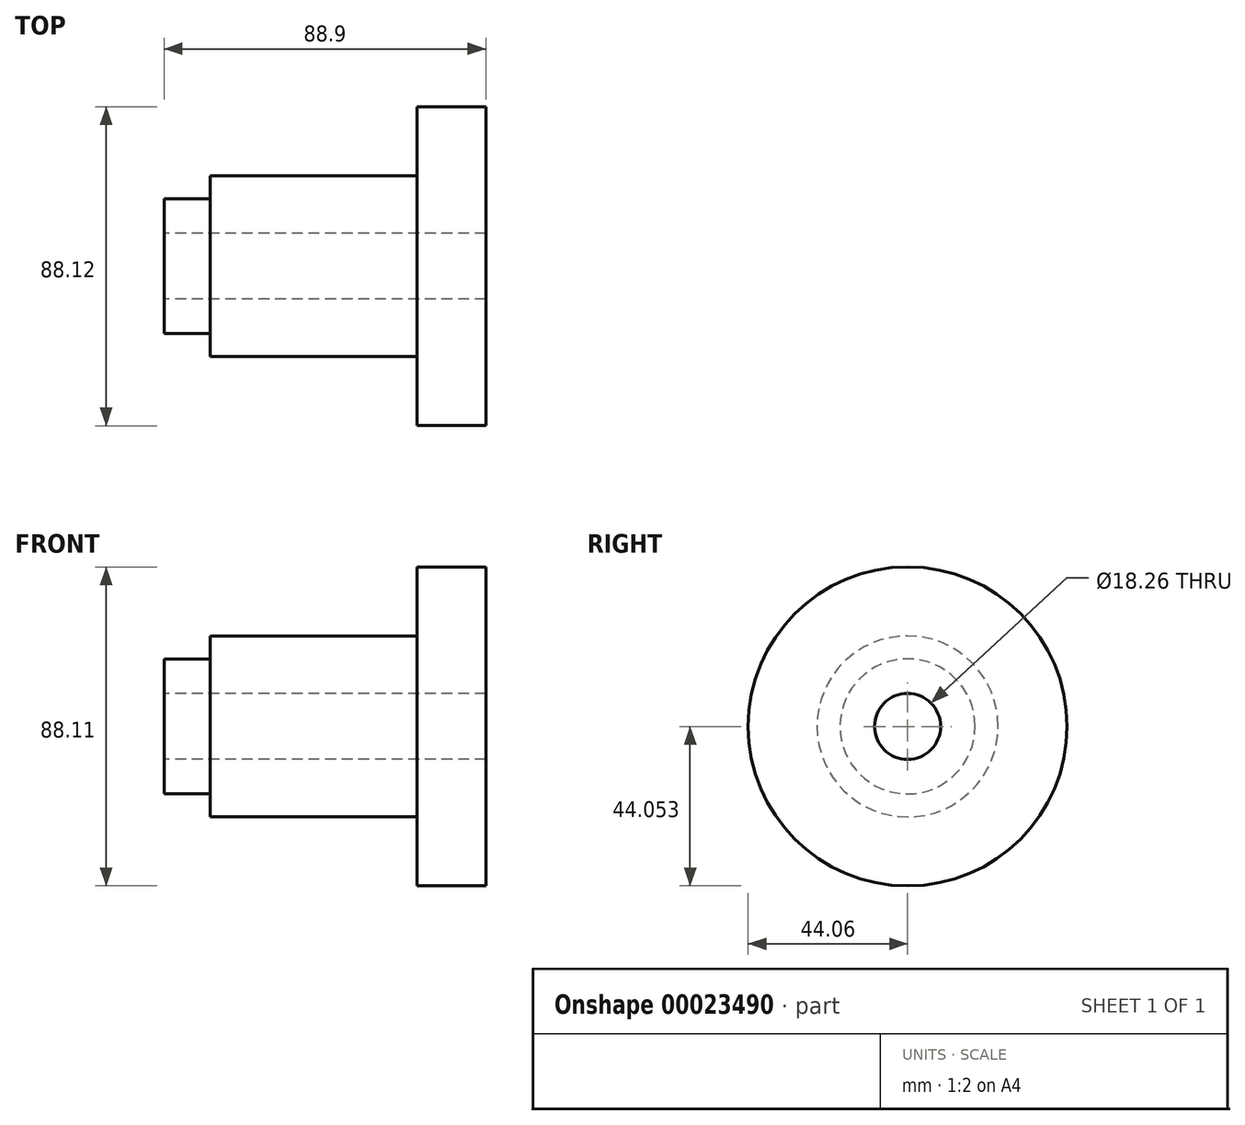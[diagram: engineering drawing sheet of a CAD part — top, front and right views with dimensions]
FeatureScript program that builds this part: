
annotation { "Feature Type Name" : "Feature", "Feature Type Description" : "" }
export const myFeature = defineFeature(function(context is Context, id is Id, definition is map)
    precondition{}
    {
        {
            var Q0;
            Q0=qCreatedBy(makeId("Front.planeOp"),FACE);
            var sketch = newSketch(context, id + "F0", { "sketchPlane" : qUnion([Q0])});
            skLineSegment(sketch, "E0.bottom", {"start": v(33.8, 9.53) * mm, "end": v(52.86, 9.53) * mm});
            skLineSegment(sketch, "E0.top", {"start": v(33.8, 44.45) * mm, "end": v(52.86, 44.45) * mm});
            skLineSegment(sketch, "E0.left", {"start": v(33.8, 9.53) * mm, "end": v(33.8, 44.45) * mm});
            skLineSegment(sketch, "E0.right", {"start": v(52.86, 9.53) * mm, "end": v(52.86, 44.45) * mm});
            skLineSegment(sketch, "E1.bottom", {"start": v(33.8, 9.53) * mm, "end": v(-23.34, 9.53) * mm});
            skLineSegment(sketch, "E1.top", {"start": v(33.8, 25.4) * mm, "end": v(-23.34, 25.4) * mm});
            skLineSegment(sketch, "E1.left", {"start": v(33.8, 9.53) * mm, "end": v(33.8, 25.4) * mm});
            skLineSegment(sketch, "E1.right", {"start": v(-23.34, 9.52) * mm, "end": v(-23.34, 25.4) * mm});
            skLineSegment(sketch, "E2.bottom", {"start": v(-23.34, 9.53) * mm, "end": v(-36.04, 9.53) * mm});
            skLineSegment(sketch, "E2.top", {"start": v(-23.34, 19.05) * mm, "end": v(-36.04, 19.05) * mm});
            skLineSegment(sketch, "E2.left", {"start": v(-23.34, 9.52) * mm, "end": v(-23.34, 19.05) * mm});
            skLineSegment(sketch, "E2.right", {"start": v(-36.04, 9.53) * mm, "end": v(-36.04, 19.05) * mm});
            skPoint(sketch, "E3.end.orphan", {"position": v(43.33, 0) * mm});
            skPoint(sketch, "E3.start.orphan", {"position": v(43.33, 9.53) * mm});
            skPoint(sketch, "E4.start.orphan", {"position": v(-255.59, 0) * mm});
            skLineSegment(sketch, "E5", {"start": v(-45.85, 0.4) * mm, "end": v(54.02, 0.4) * mm, "construction": true});
            skSolve(sketch);
        }
        {
            var Q0;
            Q0 = qSketchRegion(id + "F0", true);
            var Q1;
            Q1=sQuery(id+"F0.wireOp",EDGE,"E5");
            revolve(context, id + "F1", {"entities" : qUnion([Q0]), "axis" : qUnion([Q1]), "revolveType" : RevolveType.FULL});
        }
    });
